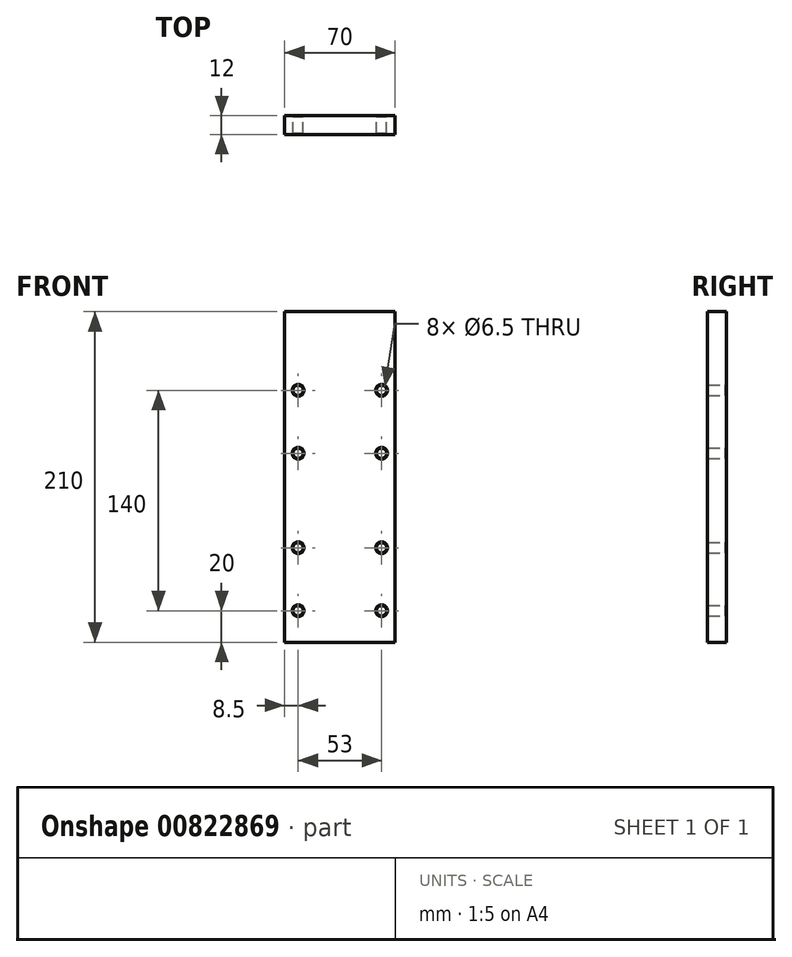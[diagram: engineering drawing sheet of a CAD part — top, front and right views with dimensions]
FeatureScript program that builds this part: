
annotation { "Feature Type Name" : "Feature", "Feature Type Description" : "" }
export const myFeature = defineFeature(function(context is Context, id is Id, definition is map)
    precondition{}
    {
        {
            var Q0;
            Q0=qCreatedBy(makeId("Front.planeOp"),FACE);
            var sketch = newSketch(context, id + "F0", { "sketchPlane" : qUnion([Q0])});
            skLineSegment(sketch, "E0.bottom", {"start": v(-35, -105) * mm, "end": v(35, -105) * mm});
            skLineSegment(sketch, "E0.top", {"start": v(-35, 105) * mm, "end": v(35, 105) * mm});
            skLineSegment(sketch, "E0.left", {"start": v(-35, -105) * mm, "end": v(-35, 105) * mm});
            skLineSegment(sketch, "E0.right", {"start": v(35, -105) * mm, "end": v(35, 105) * mm});
            skPoint(sketch, "E0.middle", {"position": v(0, 0) * mm});
            skLineSegment(sketch, "E1", {"start": v(0, 0) * mm, "end": v(0, 61.02) * mm, "construction": true});
            skLineSegment(sketch, "E2.bottom", {"start": v(-26.5, 15) * mm, "end": v(26.5, 15) * mm, "construction": true});
            skLineSegment(sketch, "E2.top", {"start": v(-26.5, 55) * mm, "end": v(26.5, 55) * mm, "construction": true});
            skLineSegment(sketch, "E2.left", {"start": v(-26.5, 15) * mm, "end": v(-26.5, 55) * mm, "construction": true});
            skLineSegment(sketch, "E2.right", {"start": v(26.5, 15) * mm, "end": v(26.5, 55) * mm, "construction": true});
            skPoint(sketch, "E2.middle", {"position": v(0, 35) * mm});
            skCircle(sketch, "E3", {"center": v(-26.5, 55) * mm, "radius": 3.25 * mm});
            skCircle(sketch, "E4", {"center": v(-26.5, 15) * mm, "radius": 3.25 * mm});
            skCircle(sketch, "E5", {"center": v(26.5, 15) * mm, "radius": 3.25 * mm});
            skCircle(sketch, "E6", {"center": v(26.5, 55) * mm, "radius": 3.25 * mm});
            skLineSegment(sketch, "E7.0.1.0", {"start": v(-26.5, -45) * mm, "end": v(26.5, -45) * mm, "construction": true});
            skLineSegment(sketch, "E7.0.1.1", {"start": v(-26.5, -85) * mm, "end": v(-26.5, -45) * mm, "construction": true});
            skLineSegment(sketch, "E7.0.1.2", {"start": v(-26.5, -85) * mm, "end": v(26.5, -85) * mm, "construction": true});
            skLineSegment(sketch, "E7.0.1.3", {"start": v(26.5, -85) * mm, "end": v(26.5, -45) * mm, "construction": true});
            skCircle(sketch, "E7.0.1.4", {"center": v(26.5, -45) * mm, "radius": 3.25 * mm});
            skCircle(sketch, "E7.0.1.5", {"center": v(26.5, -85) * mm, "radius": 3.25 * mm});
            skCircle(sketch, "E7.0.1.6", {"center": v(-26.5, -85) * mm, "radius": 3.25 * mm});
            skCircle(sketch, "E7.0.1.7", {"center": v(-26.5, -45) * mm, "radius": 3.25 * mm});
            skLineSegment(sketch, "E7.direction1", {"start": v(-26.5, 15) * mm, "end": v(-1.5, 15) * mm, "construction": true});
            skLineSegment(sketch, "E7.direction2", {"start": v(-26.5, 15) * mm, "end": v(-26.5, -85) * mm, "construction": true});
            skSolve(sketch);
        }
        {
            var Q0;
            Q0 = qSketchRegion(id + "F0", true);
            extrude(context, id + "F1", {"entities" : qUnion([Q0]), "depth" : 12 * mm, "offsetDistance" : 25 * mm});
        }
        {
            var Q0;
            Q0=makeQuery(id+"F1.opExtrude","SWEPT_FACE",FACE,{"disambiguationData":[OSD([sQuery(id+"F0.wireOp",EDGE,"E3")])]});
            var Q1;
            Q1=makeQuery(id+"F1.opExtrude","SWEPT_FACE",FACE,{"disambiguationData":[OSD([sQuery(id+"F0.wireOp",EDGE,"E4")])]});
            var Q2;
            Q2=makeQuery(id+"F1.opExtrude","SWEPT_FACE",FACE,{"disambiguationData":[OSD([sQuery(id+"F0.wireOp",EDGE,"E6")])]});
            var Q3;
            Q3=makeQuery(id+"F1.opExtrude","SWEPT_FACE",FACE,{"disambiguationData":[OSD([sQuery(id+"F0.wireOp",EDGE,"E5")])]});
            var Q4;
            Q4=makeQuery(id+"F1.opExtrude","SWEPT_FACE",FACE,{"disambiguationData":[OSD([sQuery(id+"F0.wireOp",EDGE,"E7.0.1.7")])]});
            var Q5;
            Q5=makeQuery(id+"F1.opExtrude","SWEPT_FACE",FACE,{"disambiguationData":[OSD([sQuery(id+"F0.wireOp",EDGE,"E7.0.1.6")])]});
            var Q6;
            Q6=makeQuery(id+"F1.opExtrude","SWEPT_FACE",FACE,{"disambiguationData":[OSD([sQuery(id+"F0.wireOp",EDGE,"E7.0.1.5")])]});
            var Q7;
            Q7=makeQuery(id+"F1.opExtrude","SWEPT_FACE",FACE,{"disambiguationData":[OSD([sQuery(id+"F0.wireOp",EDGE,"E7.0.1.4")])]});
            chamfer(context, id + "F2", {"entities" : qUnion([Q0, Q1, Q2, Q3, Q4, Q5, Q6, Q7]), "width" : 0.5 * mm, "tangentPropagation" : true});
        }
    });
